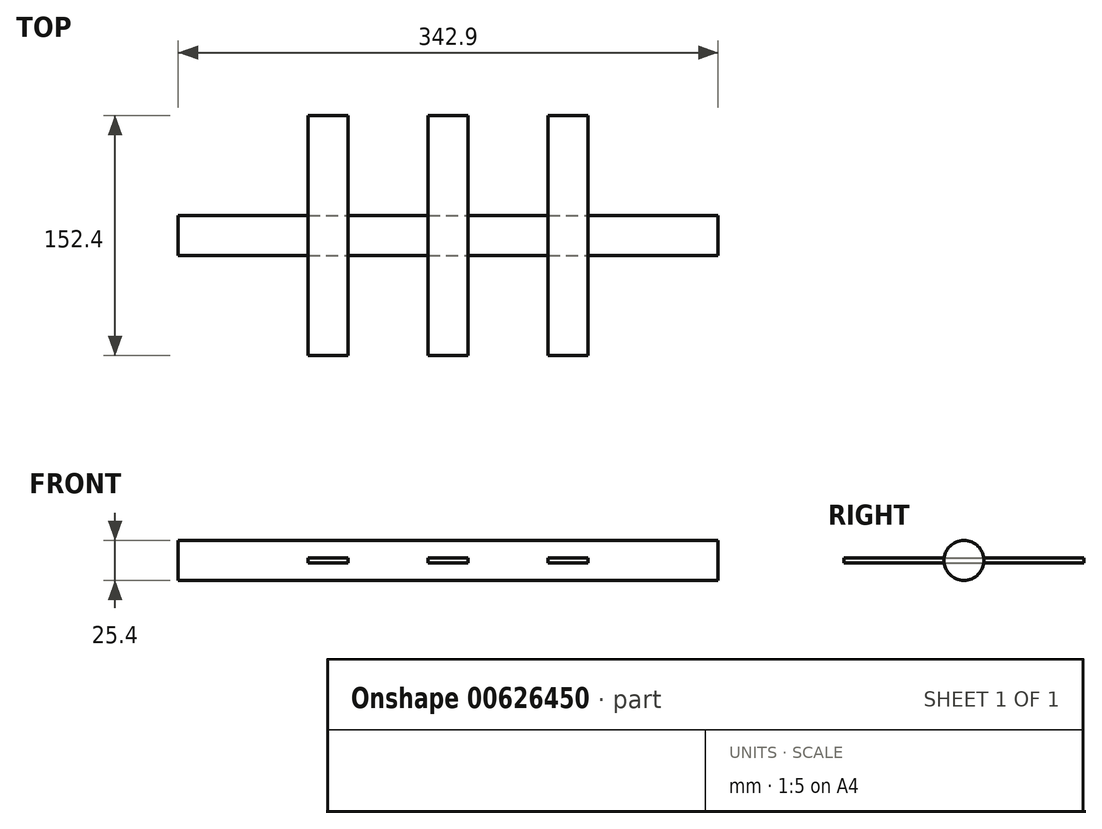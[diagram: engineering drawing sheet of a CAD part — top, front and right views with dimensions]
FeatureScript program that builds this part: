
annotation { "Feature Type Name" : "Feature", "Feature Type Description" : "" }
export const myFeature = defineFeature(function(context is Context, id is Id, definition is map)
    precondition{}
    {
        {
            var Q0;
            Q0=qCreatedBy(makeId("Front.planeOp"),FACE);
            var sketch = newSketch(context, id + "F0", { "sketchPlane" : qUnion([Q0])});
            skLineSegment(sketch, "E0.bottom", {"start": v(0, 0) * mm, "end": v(-342.9, 0) * mm});
            skLineSegment(sketch, "E0.top", {"start": v(0, 12.7) * mm, "end": v(-342.9, 12.7) * mm});
            skLineSegment(sketch, "E0.left", {"start": v(0, 0) * mm, "end": v(0, 12.7) * mm});
            skLineSegment(sketch, "E0.right", {"start": v(-342.9, 0) * mm, "end": v(-342.9, 12.7) * mm});
            skSolve(sketch);
        }
        {
            var Q0;
            Q0=makeQuery(id+"F0.imprint","IMPRINT",FACE,{"disambiguationData":[TD([[makeQuery(id+"F0.imprint","IMPRINT",EDGE,{"derivedFrom":sQuery(id+"F0.wireOp",EDGE,"E0.bottom")}),-1.0]])]});
            var sketch = newSketch(context, id + "F1", { "sketchPlane" : qUnion([Q0])});
            skLineSegment(sketch, "E1.bottom", {"start": v(-234.95, 1.59) * mm, "end": v(-260.35, 1.59) * mm});
            skLineSegment(sketch, "E1.top", {"start": v(-234.95, -1.59) * mm, "end": v(-260.35, -1.59) * mm});
            skLineSegment(sketch, "E1.left", {"start": v(-234.95, 1.59) * mm, "end": v(-234.95, -1.59) * mm});
            skLineSegment(sketch, "E1.right", {"start": v(-260.35, 1.59) * mm, "end": v(-260.35, -1.59) * mm});
            skPoint(sketch, "E1.middle", {"position": v(-247.65, 0) * mm});
            skSolve(sketch);
        }
        {
            var Q0;
            Q0=makeQuery(id+"F0.imprint","IMPRINT",FACE,{"disambiguationData":[TD([[makeQuery(id+"F0.imprint","IMPRINT",EDGE,{"derivedFrom":sQuery(id+"F0.wireOp",EDGE,"E0.bottom")}),-1.0]])]});
            var sketch = newSketch(context, id + "F2", { "sketchPlane" : qUnion([Q0])});
            skLineSegment(sketch, "E2.bottom", {"start": v(-158.75, 1.59) * mm, "end": v(-184.15, 1.59) * mm});
            skLineSegment(sketch, "E2.top", {"start": v(-158.75, -1.59) * mm, "end": v(-184.15, -1.59) * mm});
            skLineSegment(sketch, "E2.left", {"start": v(-158.75, 1.59) * mm, "end": v(-158.75, -1.59) * mm});
            skLineSegment(sketch, "E2.right", {"start": v(-184.15, 1.59) * mm, "end": v(-184.15, -1.59) * mm});
            skPoint(sketch, "E2.middle", {"position": v(-171.45, 0) * mm});
            skSolve(sketch);
        }
        {
            var Q0;
            Q0=makeQuery(id+"F0.imprint","IMPRINT",FACE,{"disambiguationData":[TD([[makeQuery(id+"F0.imprint","IMPRINT",EDGE,{"derivedFrom":sQuery(id+"F0.wireOp",EDGE,"E0.bottom")}),-1.0]])]});
            var sketch = newSketch(context, id + "F3", { "sketchPlane" : qUnion([Q0])});
            skLineSegment(sketch, "E3.bottom", {"start": v(-107.95, 1.59) * mm, "end": v(-82.55, 1.59) * mm});
            skLineSegment(sketch, "E3.top", {"start": v(-107.95, -1.59) * mm, "end": v(-82.55, -1.59) * mm});
            skLineSegment(sketch, "E3.left", {"start": v(-107.95, 1.59) * mm, "end": v(-107.95, -1.59) * mm});
            skLineSegment(sketch, "E3.right", {"start": v(-82.55, 1.59) * mm, "end": v(-82.55, -1.59) * mm});
            skPoint(sketch, "E3.middle", {"position": v(-95.25, 0) * mm});
            skSolve(sketch);
        }
        {
            var Q0;
            Q0=qSketchRegion(id+"F1",true);
            var Q1;
            Q1=qSketchRegion(id+"F2",true);
            var Q2;
            Q2=qSketchRegion(id+"F3",true);
            extrude(context, id + "F4", {"entities" : qUnion([Q0, Q1, Q2]), "endBound" : BoundingType.SYMMETRIC, "depth" : 152.4 * mm, "offsetDistance" : 25.4 * mm});
        }
        {
            var Q0;
            Q0=makeQuery(id+"F0.imprint","IMPRINT",FACE,{"disambiguationData":[TD([[makeQuery(id+"F0.imprint","IMPRINT",EDGE,{"derivedFrom":sQuery(id+"F0.wireOp",EDGE,"E0.bottom")}),-1.0]])]});
            var Q1;
            Q1=sQuery(id+"F0.wireOp",EDGE,"E0.bottom");
            revolve(context, id + "F5", {"entities" : qUnion([Q0]), "axis" : qUnion([Q1]), "revolveType" : RevolveType.FULL});
        }
    });
